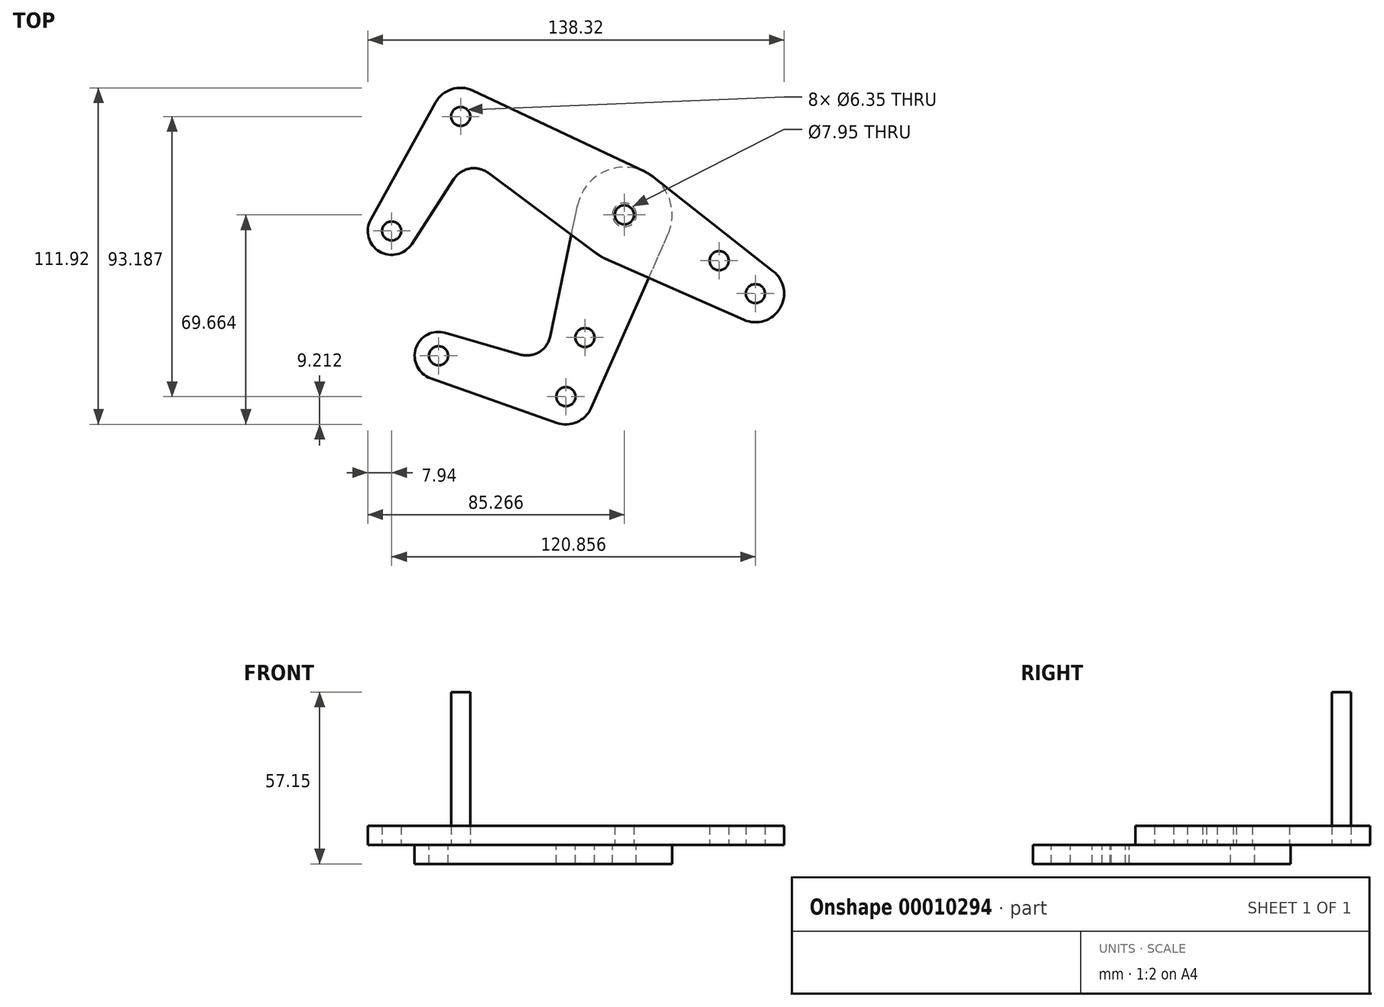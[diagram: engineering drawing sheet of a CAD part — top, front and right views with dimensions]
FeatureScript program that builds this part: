
annotation { "Feature Type Name" : "Feature", "Feature Type Description" : "" }
export const myFeature = defineFeature(function(context is Context, id is Id, definition is map)
    precondition{}
    {
        {
            var Q0;
            Q0=qCreatedBy(makeId("Top.planeOp"),FACE);
            var sketch = newSketch(context, id + "F0", { "sketchPlane" : qUnion([Q0])});
            skLineSegment(sketch, "E0", {"start": v(-37.41, 0) * mm, "end": v(-14.5, 38.09) * mm, "construction": true});
            skLineSegment(sketch, "E1", {"start": v(-14.5, 38.09) * mm, "end": v(112, -38.02) * mm, "construction": true});
            skCircle(sketch, "E2", {"center": v(-37.41, 0) * mm, "radius": 7.94 * mm});
            skCircle(sketch, "E3", {"center": v(-37.41, 0) * mm, "radius": 3.18 * mm});
            skCircle(sketch, "E4", {"center": v(-14.5, 38.09) * mm, "radius": 3.18 * mm});
            skCircle(sketch, "E5", {"center": v(-14.5, 38.09) * mm, "radius": 9.53 * mm});
            skCircle(sketch, "E6", {"center": v(39.92, 5.35) * mm, "radius": 15.88 * mm});
            skCircle(sketch, "E7", {"center": v(39.92, 5.35) * mm, "radius": 3.18 * mm});
            skCircle(sketch, "E8", {"center": v(83.45, -20.83) * mm, "radius": 3.18 * mm});
            skLineSegment(sketch, "E9", {"start": v(-44.35, 3.85) * mm, "end": v(-22.83, 42.7) * mm});
            skLineSegment(sketch, "E10", {"start": v(-10.43, 46.7) * mm, "end": v(46.7, 19.7) * mm});
            skCircle(sketch, "E11", {"center": v(83.45, -20.83) * mm, "radius": 9.53 * mm});
            skLineSegment(sketch, "E12", {"start": v(89.34, -13.35) * mm, "end": v(49.74, 17.83) * mm});
            skLineSegment(sketch, "E13", {"start": v(79.6, -29.55) * mm, "end": v(33.5, -9.17) * mm});
            skLineSegment(sketch, "E14", {"start": v(30.41, -7.36) * mm, "end": v(-5.27, 19.3) * mm});
            skLineSegment(sketch, "E15", {"start": v(-30.76, -4.33) * mm, "end": v(-16.69, 17.27) * mm});
            skLineSegment(sketch, "E16.trimOffspring", {"start": v(-19.43, 29.89) * mm, "end": v(-20.2, 30.46) * mm});
            skArc(sketch, "E17", {"start": v(-5.27, 19.3) * mm, "mid": v(-11.42, 20.76) * mm, "end": v(-16.69, 17.27) * mm});
            skCircle(sketch, "E18", {"center": v(71.4, -9.88) * mm, "radius": 3.18 * mm});
            skCircle(sketch, "E19", {"center": v(39.92, 5.35) * mm, "radius": 3.98 * mm});
            skLineSegment(sketch, "E20", {"start": v(39.92, 5.35) * mm, "end": v(20.48, -55.1) * mm, "construction": true});
            skLineSegment(sketch, "E21", {"start": v(20.48, -55.1) * mm, "end": v(-21.84, -41.5) * mm, "construction": true});
            skCircle(sketch, "E22", {"center": v(-21.84, -41.5) * mm, "radius": 3.18 * mm});
            skCircle(sketch, "E23", {"center": v(-21.84, -41.5) * mm, "radius": 7.94 * mm});
            skCircle(sketch, "E24", {"center": v(20.48, -55.1) * mm, "radius": 3.18 * mm});
            skCircle(sketch, "E25", {"center": v(20.48, -55.1) * mm, "radius": 9.2 * mm});
            skCircle(sketch, "E26", {"center": v(26.8, -35.44) * mm, "radius": 3.18 * mm});
            skLineSegment(sketch, "E27", {"start": v(-24.48, -48.98) * mm, "end": v(17.41, -63.78) * mm});
            skLineSegment(sketch, "E28", {"start": v(-19.62, -33.87) * mm, "end": v(5.26, -41.1) * mm});
            skLineSegment(sketch, "E29", {"start": v(28.9, -58.82) * mm, "end": v(54.44, -1.07) * mm});
            skLineSegment(sketch, "E30", {"start": v(11.47, -53.22) * mm, "end": v(11.67, -52.26) * mm});
            skArc(sketch, "E31", {"start": v(5.26, -41.1) * mm, "mid": v(11.57, -40.27) * mm, "end": v(15.25, -35.08) * mm});
            skLineSegment(sketch, "E32.trimOffspring", {"start": v(15.25, -35.08) * mm, "end": v(24.38, 8.6) * mm});
            skSolve(sketch);
        }
        {
            var Q0;
            {var subQ6=sQuery(id+"F0.wireOp",EDGE,"E9");Q0=makeQuery(id+"F0.imprint","IMPRINT",FACE,{"disambiguationData":[TD([[makeQuery(id+"F0.imprint","IMPRINT",EDGE,{"derivedFrom":subQ6}),-1.0]])]});}
            var Q1;
            Q1=makeQuery(id+"F0.imprint","IMPRINT",FACE,{"disambiguationData":[TD([[makeQuery(id+"F0.imprint","IMPRINT",EDGE,{"derivedFrom":sQuery(id+"F0.wireOp",EDGE,"E3")}),-1.0]])]});
            var Q2;
            Q2=makeQuery(id+"F0.imprint","IMPRINT",FACE,{"disambiguationData":[TD([[makeQuery(id+"F0.imprint","IMPRINT",EDGE,{"derivedFrom":sQuery(id+"F0.wireOp",EDGE,"E4")}),-1.0]])]});
            var Q3;
            Q3=makeQuery(id+"F0.imprint","IMPRINT",FACE,{"disambiguationData":[TD([[makeQuery(id+"F0.imprint","IMPRINT",EDGE,{"derivedFrom":sQuery(id+"F0.wireOp",EDGE,"E19")}),-1.0]])]});
            var Q4;
            {var subQ7=sQuery(id+"F0.wireOp",EDGE,"E12");Q4=makeQuery(id+"F0.imprint","IMPRINT",FACE,{"disambiguationData":[TD([[makeQuery(id+"F0.imprint","IMPRINT",EDGE,{"derivedFrom":subQ7}),1.0]])]});}
            var Q5;
            Q5=makeQuery(id+"F0.imprint","IMPRINT",FACE,{"disambiguationData":[TD([[makeQuery(id+"F0.imprint","IMPRINT",EDGE,{"derivedFrom":sQuery(id+"F0.wireOp",EDGE,"E8")}),-1.0]])]});
            var Q6;
            {var subQ1=sQuery(id+"F0.wireOp",EDGE,"E13");var subQ3=sQuery(id+"F0.wireOp",EDGE,"E6");var subQ5=makeQuery(id+"F0.imprint","INTERSECT",VERTEX,{"derivedFrom":[subQ3,subQ1]});Q6=makeQuery(id+"F0.imprint","IMPRINT",FACE,{"disambiguationData":[TD([[makeQuery(id+"F0.imprint","IMPRINT",EDGE,{"disambiguationData":[TD([[subQ5,-1.0]])],"derivedFrom":subQ3}),-1.0]])]});}
            var Q7;
            {var subQ1=sQuery(id+"F0.wireOp",EDGE,"E14");var subQ3=sQuery(id+"F0.wireOp",EDGE,"E6");var subQ5=makeQuery(id+"F0.imprint","INTERSECT",VERTEX,{"derivedFrom":[subQ3,subQ1]});Q7=makeQuery(id+"F0.imprint","IMPRINT",FACE,{"disambiguationData":[TD([[makeQuery(id+"F0.imprint","IMPRINT",EDGE,{"disambiguationData":[TD([[subQ5,1.0]])],"derivedFrom":subQ3}),-1.0]])]});}
            var Q8;
            Q8=makeQuery(id+"F0.imprint","IMPRINT",FACE,{"disambiguationData":[TD([[makeQuery(id+"F0.imprint","IMPRINT",EDGE,{"derivedFrom":sQuery(id+"F0.wireOp",EDGE,"E7")}),-1.0]])]});
            extrude(context, id + "F1", {"entities" : qUnion([Q0, Q1, Q2, Q3, Q4, Q5, Q6, Q7, Q8]), "depth" : 6.35 * mm});
        }
        {
            var Q0;
            Q0=makeQuery(id+"F0.imprint","IMPRINT",FACE,{"disambiguationData":[TD([[makeQuery(id+"F0.imprint","IMPRINT",EDGE,{"derivedFrom":sQuery(id+"F0.wireOp",EDGE,"E22")}),-1.0]])]});
            var Q1;
            Q1=makeQuery(id+"F0.imprint","IMPRINT",FACE,{"disambiguationData":[TD([[makeQuery(id+"F0.imprint","IMPRINT",EDGE,{"derivedFrom":sQuery(id+"F0.wireOp",EDGE,"E26")}),-1.0]])]});
            var Q2;
            Q2=makeQuery(id+"F0.imprint","IMPRINT",FACE,{"disambiguationData":[TD([[makeQuery(id+"F0.imprint","IMPRINT",EDGE,{"derivedFrom":sQuery(id+"F0.wireOp",EDGE,"E24")}),-1.0]])]});
            var Q3;
            Q3=makeQuery(id+"F0.imprint","IMPRINT",FACE,{"disambiguationData":[TD([[makeQuery(id+"F0.imprint","IMPRINT",EDGE,{"derivedFrom":sQuery(id+"F0.wireOp",EDGE,"E19")}),-1.0]])]});
            var Q4;
            {var subQ1=sQuery(id+"F0.wireOp",EDGE,"E13");var subQ3=sQuery(id+"F0.wireOp",EDGE,"E6");var subQ5=makeQuery(id+"F0.imprint","INTERSECT",VERTEX,{"derivedFrom":[subQ3,subQ1]});Q4=makeQuery(id+"F0.imprint","IMPRINT",FACE,{"disambiguationData":[TD([[makeQuery(id+"F0.imprint","IMPRINT",EDGE,{"disambiguationData":[TD([[subQ5,-1.0]])],"derivedFrom":subQ3}),-1.0]])]});}
            var Q5;
            {var subQ1=sQuery(id+"F0.wireOp",EDGE,"E14");var subQ3=sQuery(id+"F0.wireOp",EDGE,"E6");var subQ5=makeQuery(id+"F0.imprint","INTERSECT",VERTEX,{"derivedFrom":[subQ3,subQ1]});Q5=makeQuery(id+"F0.imprint","IMPRINT",FACE,{"disambiguationData":[TD([[makeQuery(id+"F0.imprint","IMPRINT",EDGE,{"disambiguationData":[TD([[subQ5,1.0]])],"derivedFrom":subQ3}),-1.0]])]});}
            extrude(context, id + "F2", {"entities" : qUnion([Q0, Q1, Q2, Q3, Q4, Q5]), "oppositeDirection" : true, "depth" : 6.35 * mm});
        }
        {
            var Q0;
            Q0=makeQuery(id+"F0.imprint","IMPRINT",FACE,{"disambiguationData":[TD([[makeQuery(id+"F0.imprint","IMPRINT",EDGE,{"derivedFrom":sQuery(id+"F0.wireOp",EDGE,"E4")}),1.0]])]});
            extrude(context, id + "F3", {"entities" : qUnion([Q0]), "depth" : 50.8 * mm});
        }
    });
